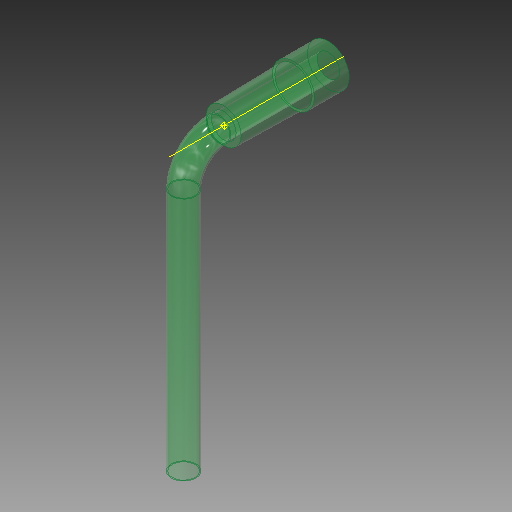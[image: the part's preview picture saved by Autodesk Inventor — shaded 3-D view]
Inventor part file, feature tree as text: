
AUTODESK INVENTOR PART (.ipt)
format: ipt  version: 2019 (Build 230136000, 136)  size: 144,896 bytes
history: native  units: mm
features: other x7, sketch x4, extrude x2, sweep x1
ambient origin geometry x8: Origin, YZ Plane, XZ Plane, XY Plane, X Axis, Y Axis, Z Axis, Center Point
bodies: Body1 (feature_tree)
feature tree (14):
  other  "Sólido1"
  extrude  "Extrusão1"  Depth=10.0mm TaperAngle=0.0deg
  extrude  "Extrusão2"  Depth=20.0mm TaperAngle=0.0deg
  other  "Face para inclinação de faces1"
  sketch  "Esboço3"  dims[d8=80.0mm d9=10.0mm d10=0.0mm d11=0.0mm]
  other  "Ponto de trabalho1"
  sketch  "Esboço 3D1"  dims[d0=12.0mm d1=10.0mm d2=0.0mm]
  other  "Eixo de trabalho1"
  sweep  "Varredura1"
  sketch  "Esboço1"  dims[d3=1.0mm d4=20.0mm d5=0.0mm]
  other  "Referência1"
  sketch  "Esboço2"  dims[d6=0.174533mm d7=0.3mm]
  other  "Conjunto Ambu.iam"
  other  "Tampa de Entrada:1"
